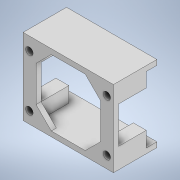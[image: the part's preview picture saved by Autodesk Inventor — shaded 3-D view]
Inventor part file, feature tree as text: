
AUTODESK INVENTOR PART (.ipt)
format: ipt  version: 2021 (Build 250183000, 183)  size: 177,152 bytes
history: native  units: in
note: dims shown in document units (in); Inventor stores cm internally (conversion verified against a paired STEP export)
features: plane x3, extrude x3, other x3, sketch x2
ambient origin geometry x8: Origin, YZ Plane, XZ Plane, XY Plane, X Axis, Y Axis, Z Axis, Center Point
bodies: Solid1 (feature_tree)
feature tree (11):
  plane  "Work Plane1"
  sketch  "Sketch1"  dims[d17=0.3937in d18=0.0in d19=0.0787in]
  plane  "Work Plane2"
  extrude  "Extrusion1"  Depth=0.0787in
  sketch  "Sketch2"  dims[d20=0.0787in d21=0.2362in d22=0.2362in d23=0.2362in d24=0.2362in d25=0.2362in d26=0.2362in d27=0.2362in d28=0.2362in d29=0.0787in d30=0.0in d31=0.0787in d32=0.0in]
  extrude  "Extrusion2"  Depth=0.0787in
  plane  "Work Plane3"
  extrude  "Extrusion3"  Depth=0.0787in
  parser-record x1  (decoder bookkeeping rows leaked as tree rows — omitted from the tree; the rows remain in map.json)
  other  "assembly.iam"
  other  "GPS_ublox_board:1"
note: 1 file-system path scrubbed to <path> (originals preserved in map.json)
